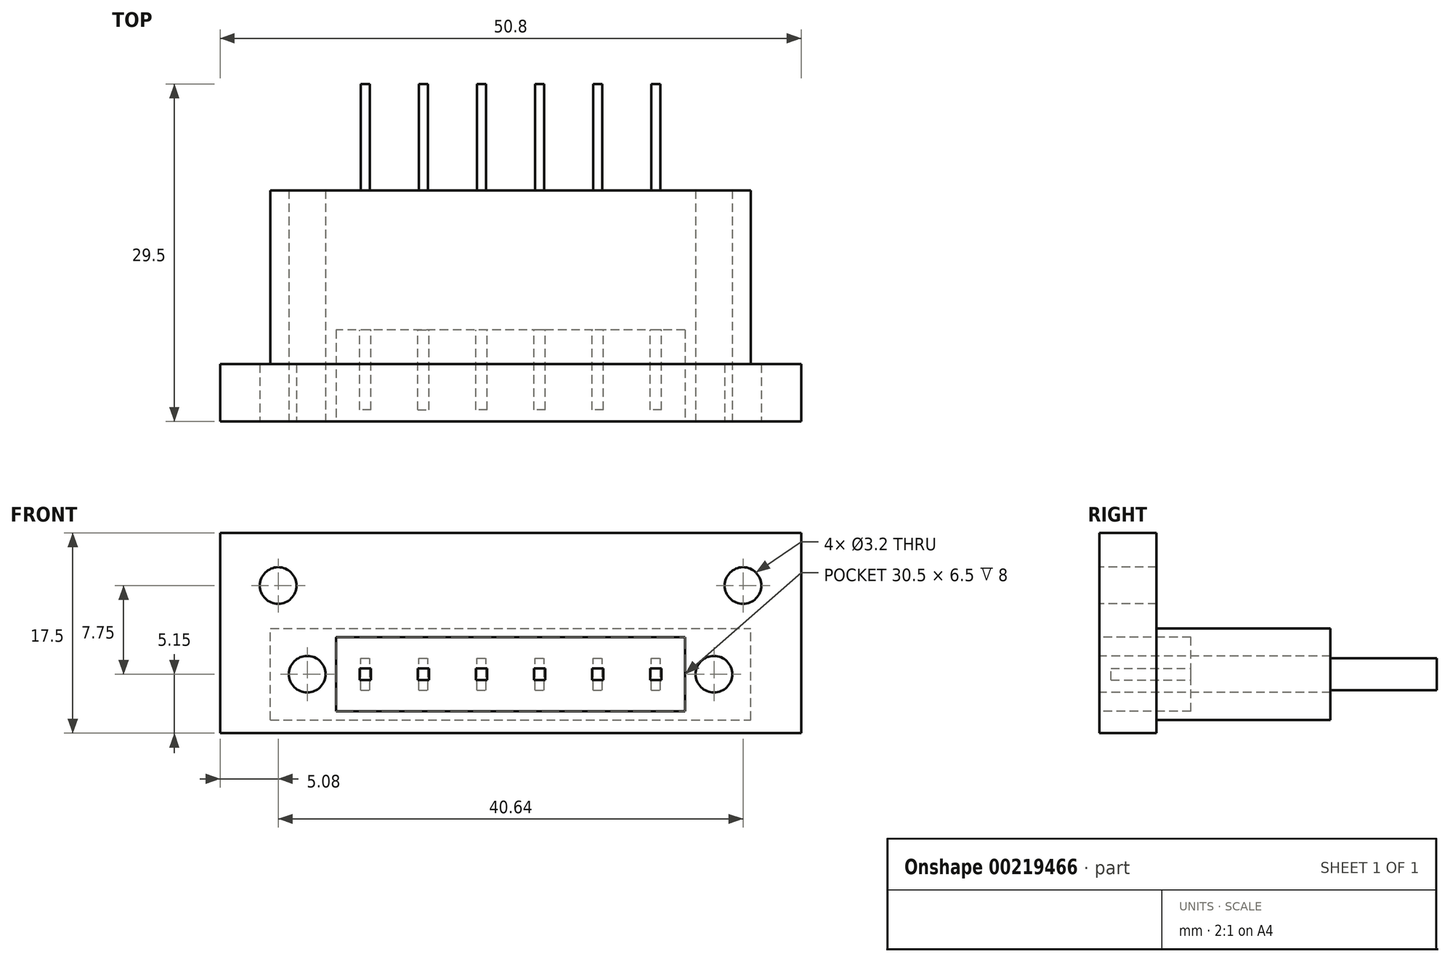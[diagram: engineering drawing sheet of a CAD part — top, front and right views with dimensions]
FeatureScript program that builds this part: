
annotation { "Feature Type Name" : "Feature", "Feature Type Description" : "" }
export const myFeature = defineFeature(function(context is Context, id is Id, definition is map)
    precondition{}
    {
        {
            var Q0;
            Q0=qCreatedBy(makeId("Front.planeOp"),FACE);
            var sketch = newSketch(context, id + "F0", { "sketchPlane" : qUnion([Q0])});
            skLineSegment(sketch, "E0.bottom", {"start": v(-25.4, -8.75) * mm, "end": v(25.4, -8.75) * mm});
            skLineSegment(sketch, "E0.top", {"start": v(-25.4, 8.75) * mm, "end": v(25.4, 8.75) * mm});
            skLineSegment(sketch, "E0.left", {"start": v(-25.4, -8.75) * mm, "end": v(-25.4, 8.75) * mm});
            skLineSegment(sketch, "E0.right", {"start": v(25.4, -8.75) * mm, "end": v(25.4, 8.75) * mm});
            skPoint(sketch, "E0.middle", {"position": v(0, 0) * mm});
            skSolve(sketch);
        }
        {
            var Q0;
            Q0=qSketchRegion(id+"F0",true);
            extrude(context, id + "F1", {"entities" : qUnion([Q0]), "depth" : 5 * mm});
        }
        {
            var Q0;
            Q0=makeQuery(id+"F1.opExtrude","CAP_FACE",FACE,{"disambiguationData":[OSD([sQuery(id+"F0.wireOp",EDGE,"E0.bottom"),sQuery(id+"F0.wireOp",EDGE,"E0.top"),sQuery(id+"F0.wireOp",EDGE,"E0.left"),sQuery(id+"F0.wireOp",EDGE,"E0.right")])],"isStart":false});
            var sketch = newSketch(context, id + "F2", { "sketchPlane" : qUnion([Q0])});
            skLineSegment(sketch, "E1.bottom", {"start": v(15.25, -6.85) * mm, "end": v(-15.25, -6.85) * mm});
            skLineSegment(sketch, "E1.top", {"start": v(15.25, -0.35) * mm, "end": v(-15.25, -0.35) * mm});
            skLineSegment(sketch, "E1.left", {"start": v(15.25, -6.85) * mm, "end": v(15.25, -0.35) * mm});
            skLineSegment(sketch, "E1.right", {"start": v(-15.25, -6.85) * mm, "end": v(-15.25, -0.35) * mm});
            skPoint(sketch, "E1.middle", {"position": v(0, -3.6) * mm});
            skSolve(sketch);
        }
        {
            var Q0;
            Q0=makeQuery(id+"F1.opExtrude","CAP_FACE",FACE,{"disambiguationData":[OSD([sQuery(id+"F0.wireOp",EDGE,"E0.bottom"),sQuery(id+"F0.wireOp",EDGE,"E0.top"),sQuery(id+"F0.wireOp",EDGE,"E0.left"),sQuery(id+"F0.wireOp",EDGE,"E0.right")])],"isStart":true});
            var sketch = newSketch(context, id + "F3", { "sketchPlane" : qUnion([Q0])});
            skLineSegment(sketch, "E2.bottom", {"start": v(21, -7.6) * mm, "end": v(-21, -7.6) * mm});
            skLineSegment(sketch, "E2.top", {"start": v(21, 0.4) * mm, "end": v(-21, 0.4) * mm});
            skLineSegment(sketch, "E2.left", {"start": v(21, -7.6) * mm, "end": v(21, 0.4) * mm});
            skLineSegment(sketch, "E2.right", {"start": v(-21, -7.6) * mm, "end": v(-21, 0.4) * mm});
            skPoint(sketch, "E2.middle", {"position": v(0, -3.6) * mm});
            skSolve(sketch);
        }
        {
            var Q0;
            Q0=qSketchRegion(id+"F3",true);
            extrude(context, id + "F4", {"entities" : qUnion([Q0]), "operationType" : NewBodyOperationType.ADD, "depth" : 15.2 * mm});
        }
        {
            var Q0;
            Q0=qSketchRegion(id+"F2",true);
            extrude(context, id + "F5", {"entities" : qUnion([Q0]), "operationType" : NewBodyOperationType.REMOVE, "oppositeDirection" : true, "depth" : 8 * mm});
        }
        {
            var Q0;
            Q0=makeQuery(id+"F1.opExtrude","CAP_FACE",FACE,{"disambiguationData":[OSD([sQuery(id+"F0.wireOp",EDGE,"E0.bottom"),sQuery(id+"F0.wireOp",EDGE,"E0.top"),sQuery(id+"F0.wireOp",EDGE,"E0.left"),sQuery(id+"F0.wireOp",EDGE,"E0.right")])],"isStart":false});
            var sketch = newSketch(context, id + "F6", { "sketchPlane" : qUnion([Q0])});
            skPoint(sketch, "E3", {"position": v(-20.32, 4.15) * mm});
            skPoint(sketch, "E4", {"position": v(20.32, 4.15) * mm});
            skPoint(sketch, "E5", {"position": v(-17.78, -3.6) * mm});
            skPoint(sketch, "E5.positionSnap0", {"position": v(-15.25, -3.6) * mm});
            skPoint(sketch, "E6", {"position": v(17.78, -3.6) * mm});
            skPoint(sketch, "E6.positionSnap0", {"position": v(15.25, -3.6) * mm});
            skSolve(sketch);
        }
        {
            var Q0;
            Q0=sQuery(id+"F6.wireOp",VERTEX,"E3");
            var Q1;
            Q1=sQuery(id+"F6.wireOp",VERTEX,"E5");
            var Q2;
            Q2=sQuery(id+"F6.wireOp",VERTEX,"E4");
            var Q3;
            Q3=sQuery(id+"F6.wireOp",VERTEX,"E6");
            var Q4;
            Q4=makeQuery(id+"F1.opExtrude","SWEPT_BODY",BODY,{"disambiguationData":[OSD([sQuery(id+"F0.wireOp",EDGE,"E0.bottom"),sQuery(id+"F0.wireOp",EDGE,"E0.top"),sQuery(id+"F0.wireOp",EDGE,"E0.left"),sQuery(id+"F0.wireOp",EDGE,"E0.right")])]});
            hole(context, id + "F7", {"style" : HoleStyle.SIMPLE, "endStyle" : HoleEndStyle.THROUGH, "holeDiameter" : 3.2 * mm, "startFromSketch" : true, "locations" : qUnion([Q0, Q1, Q2, Q3]), "scope" : qUnion([Q4]), "isTappedThrough" : true});
        }
        {
            var Q0;
            Q0=makeQuery(id+"F5.boolean.opBoolean","COPY",FACE,{"derivedFrom":makeQuery(id+"F5.opExtrude","CAP_FACE",FACE,{"disambiguationData":[OSD([sQuery(id+"F2.wireOp",EDGE,"E1.bottom"),sQuery(id+"F2.wireOp",EDGE,"E1.top"),sQuery(id+"F2.wireOp",EDGE,"E1.left"),sQuery(id+"F2.wireOp",EDGE,"E1.right")])],"isStart":false})});
            var sketch = newSketch(context, id + "F8", { "sketchPlane" : qUnion([Q0])});
            skLineSegment(sketch, "E7.bottom", {"start": v(-12.2, -4.1) * mm, "end": v(-13.2, -4.1) * mm});
            skLineSegment(sketch, "E7.top", {"start": v(-12.2, -3.1) * mm, "end": v(-13.2, -3.1) * mm});
            skLineSegment(sketch, "E7.left", {"start": v(-12.2, -4.1) * mm, "end": v(-12.2, -3.1) * mm});
            skLineSegment(sketch, "E7.right", {"start": v(-13.2, -4.1) * mm, "end": v(-13.2, -3.1) * mm});
            skPoint(sketch, "E7.middle", {"position": v(-12.7, -3.6) * mm});
            skPoint(sketch, "E7.middle.positionSnap0", {"position": v(-15.25, -3.6) * mm});
            skPoint(sketch, "E7.centerSnap0", {"position": v(-15.25, -3.6) * mm});
            skLineSegment(sketch, "E8.bottom", {"start": v(-8.12, -4.1) * mm, "end": v(-7.12, -4.1) * mm});
            skLineSegment(sketch, "E8.top", {"start": v(-8.12, -3.1) * mm, "end": v(-7.12, -3.1) * mm});
            skLineSegment(sketch, "E8.left", {"start": v(-8.12, -4.1) * mm, "end": v(-8.12, -3.1) * mm});
            skLineSegment(sketch, "E8.right", {"start": v(-7.12, -4.1) * mm, "end": v(-7.12, -3.1) * mm});
            skPoint(sketch, "E8.middle", {"position": v(-7.62, -3.6) * mm});
            skLineSegment(sketch, "E9.bottom", {"start": v(3.04, -4.1) * mm, "end": v(2.04, -4.1) * mm});
            skLineSegment(sketch, "E9.top", {"start": v(3.04, -3.1) * mm, "end": v(2.04, -3.1) * mm});
            skLineSegment(sketch, "E9.left", {"start": v(3.04, -4.1) * mm, "end": v(3.04, -3.1) * mm});
            skLineSegment(sketch, "E9.right", {"start": v(2.04, -4.1) * mm, "end": v(2.04, -3.1) * mm});
            skPoint(sketch, "E9.middle", {"position": v(2.54, -3.6) * mm});
            skPoint(sketch, "E9.middle.positionSnap0", {"position": v(-7.12, -3.6) * mm});
            skPoint(sketch, "E9.centerSnap0", {"position": v(-7.12, -3.6) * mm});
            skLineSegment(sketch, "E10.bottom", {"start": v(-2.04, -4.1) * mm, "end": v(-3.04, -4.1) * mm});
            skLineSegment(sketch, "E10.top", {"start": v(-2.04, -3.1) * mm, "end": v(-3.04, -3.1) * mm});
            skLineSegment(sketch, "E10.left", {"start": v(-2.04, -4.1) * mm, "end": v(-2.04, -3.1) * mm});
            skLineSegment(sketch, "E10.right", {"start": v(-3.04, -4.1) * mm, "end": v(-3.04, -3.1) * mm});
            skPoint(sketch, "E10.middle", {"position": v(-2.54, -3.6) * mm});
            skPoint(sketch, "E10.middle.positionSnap0", {"position": v(3.04, -3.6) * mm});
            skPoint(sketch, "E10.centerSnap0", {"position": v(3.04, -3.6) * mm});
            skLineSegment(sketch, "E11.bottom", {"start": v(8.12, -4.1) * mm, "end": v(7.12, -4.1) * mm});
            skLineSegment(sketch, "E11.top", {"start": v(8.12, -3.1) * mm, "end": v(7.12, -3.1) * mm});
            skLineSegment(sketch, "E11.left", {"start": v(8.12, -4.1) * mm, "end": v(8.12, -3.1) * mm});
            skLineSegment(sketch, "E11.right", {"start": v(7.12, -4.1) * mm, "end": v(7.12, -3.1) * mm});
            skPoint(sketch, "E11.middle", {"position": v(7.62, -3.6) * mm});
            skPoint(sketch, "E11.middle.positionSnap0", {"position": v(-2.04, -3.6) * mm});
            skPoint(sketch, "E11.centerSnap0", {"position": v(-2.04, -3.6) * mm});
            skLineSegment(sketch, "E12.bottom", {"start": v(13.2, -4.1) * mm, "end": v(12.2, -4.1) * mm});
            skLineSegment(sketch, "E12.top", {"start": v(13.2, -3.1) * mm, "end": v(12.2, -3.1) * mm});
            skLineSegment(sketch, "E12.left", {"start": v(13.2, -4.1) * mm, "end": v(13.2, -3.1) * mm});
            skLineSegment(sketch, "E12.right", {"start": v(12.2, -4.1) * mm, "end": v(12.2, -3.1) * mm});
            skPoint(sketch, "E12.middle", {"position": v(12.7, -3.6) * mm});
            skPoint(sketch, "E12.middle.positionSnap0", {"position": v(8.12, -3.6) * mm});
            skPoint(sketch, "E12.centerSnap0", {"position": v(8.12, -3.6) * mm});
            skSolve(sketch);
        }
        {
            var Q0;
            Q0=qSketchRegion(id+"F8",true);
            extrude(context, id + "F9", {"entities" : qUnion([Q0]), "depth" : 7 * mm});
        }
        {
            var Q0;
            Q0=makeQuery(id+"F4.opExtrude","CAP_FACE",FACE,{"disambiguationData":[OSD([sQuery(id+"F3.wireOp",EDGE,"E2.bottom"),sQuery(id+"F3.wireOp",EDGE,"E2.top"),sQuery(id+"F3.wireOp",EDGE,"E2.left"),sQuery(id+"F3.wireOp",EDGE,"E2.right")])],"isStart":false});
            var sketch = newSketch(context, id + "F10", { "sketchPlane" : qUnion([Q0])});
            skLineSegment(sketch, "E13.bottom", {"start": v(-12.3, -5) * mm, "end": v(-13.1, -5) * mm});
            skLineSegment(sketch, "E13.top", {"start": v(-12.3, -2.2) * mm, "end": v(-13.1, -2.2) * mm});
            skLineSegment(sketch, "E13.left", {"start": v(-12.3, -5) * mm, "end": v(-12.3, -2.2) * mm});
            skLineSegment(sketch, "E13.right", {"start": v(-13.1, -5) * mm, "end": v(-13.1, -2.2) * mm});
            skPoint(sketch, "E13.middle", {"position": v(-12.7, -3.6) * mm});
            skPoint(sketch, "E13.middle.positionSnap0", {"position": v(-21, -3.6) * mm});
            skPoint(sketch, "E13.centerSnap0", {"position": v(-21, -3.6) * mm});
            skLineSegment(sketch, "E14.bottom", {"start": v(-7.21, -5) * mm, "end": v(-8.03, -5) * mm});
            skLineSegment(sketch, "E14.top", {"start": v(-7.21, -2.2) * mm, "end": v(-8.03, -2.2) * mm});
            skLineSegment(sketch, "E14.left", {"start": v(-7.21, -5) * mm, "end": v(-7.21, -2.2) * mm});
            skLineSegment(sketch, "E14.right", {"start": v(-8.03, -5) * mm, "end": v(-8.03, -2.2) * mm});
            skPoint(sketch, "E14.middle", {"position": v(-7.62, -3.6) * mm});
            skLineSegment(sketch, "E15.bottom", {"start": v(-2.13, -5) * mm, "end": v(-2.95, -5) * mm});
            skLineSegment(sketch, "E15.top", {"start": v(-2.13, -2.2) * mm, "end": v(-2.95, -2.2) * mm});
            skLineSegment(sketch, "E15.left", {"start": v(-2.13, -5) * mm, "end": v(-2.13, -2.2) * mm});
            skLineSegment(sketch, "E15.right", {"start": v(-2.95, -5) * mm, "end": v(-2.95, -2.2) * mm});
            skPoint(sketch, "E15.middle", {"position": v(-2.54, -3.6) * mm});
            skPoint(sketch, "E15.middle.positionSnap0", {"position": v(-7.21, -3.6) * mm});
            skPoint(sketch, "E15.centerSnap0", {"position": v(-7.21, -3.6) * mm});
            skLineSegment(sketch, "E16.bottom", {"start": v(2.95, -5) * mm, "end": v(2.13, -5) * mm});
            skLineSegment(sketch, "E16.top", {"start": v(2.95, -2.2) * mm, "end": v(2.13, -2.2) * mm});
            skLineSegment(sketch, "E16.left", {"start": v(2.95, -5) * mm, "end": v(2.95, -2.2) * mm});
            skLineSegment(sketch, "E16.right", {"start": v(2.13, -5) * mm, "end": v(2.13, -2.2) * mm});
            skPoint(sketch, "E16.middle", {"position": v(2.54, -3.6) * mm});
            skPoint(sketch, "E16.middle.positionSnap0", {"position": v(-2.13, -3.6) * mm});
            skPoint(sketch, "E16.centerSnap0", {"position": v(-2.13, -3.6) * mm});
            skLineSegment(sketch, "E17.bottom", {"start": v(8.03, -5) * mm, "end": v(7.21, -5) * mm});
            skLineSegment(sketch, "E17.top", {"start": v(8.03, -2.2) * mm, "end": v(7.21, -2.2) * mm});
            skLineSegment(sketch, "E17.left", {"start": v(8.03, -5) * mm, "end": v(8.03, -2.2) * mm});
            skLineSegment(sketch, "E17.right", {"start": v(7.21, -5) * mm, "end": v(7.21, -2.2) * mm});
            skPoint(sketch, "E17.middle", {"position": v(7.62, -3.6) * mm});
            skLineSegment(sketch, "E18.bottom", {"start": v(13.1, -5) * mm, "end": v(12.3, -5) * mm});
            skLineSegment(sketch, "E18.top", {"start": v(13.1, -2.2) * mm, "end": v(12.3, -2.2) * mm});
            skLineSegment(sketch, "E18.left", {"start": v(13.1, -5) * mm, "end": v(13.1, -2.2) * mm});
            skLineSegment(sketch, "E18.right", {"start": v(12.3, -5) * mm, "end": v(12.3, -2.2) * mm});
            skPoint(sketch, "E18.middle", {"position": v(12.7, -3.6) * mm});
            skSolve(sketch);
        }
        {
            var Q0;
            Q0=qSketchRegion(id+"F10",true);
            extrude(context, id + "F11", {"entities" : qUnion([Q0]), "depth" : 9.3 * mm});
        }
    });
